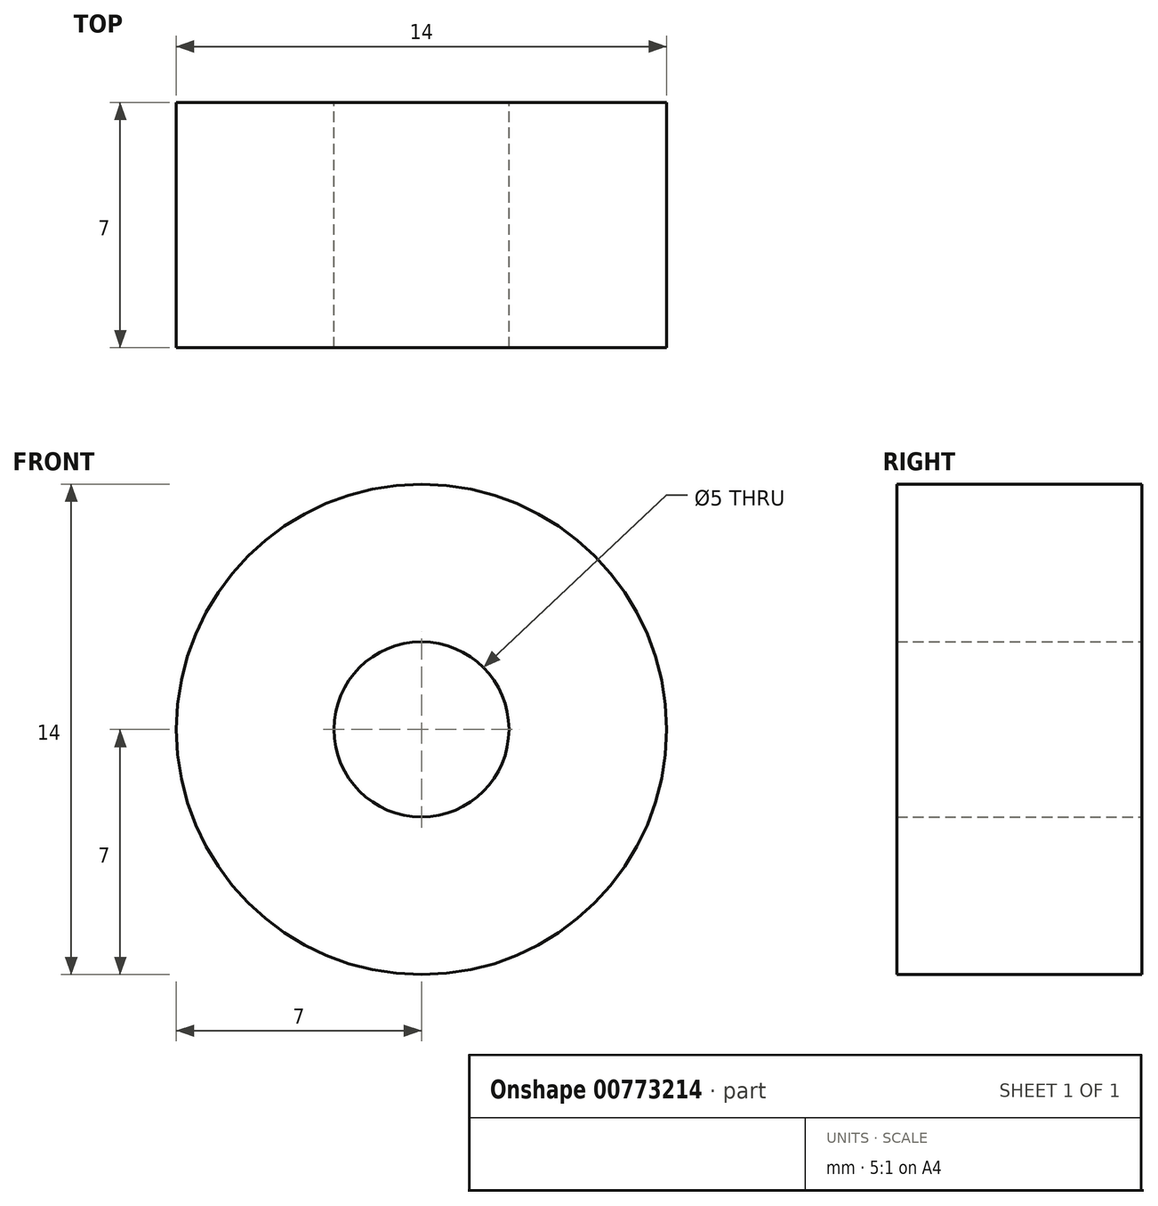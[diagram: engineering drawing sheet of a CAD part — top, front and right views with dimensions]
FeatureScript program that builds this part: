
annotation { "Feature Type Name" : "Feature", "Feature Type Description" : "" }
export const myFeature = defineFeature(function(context is Context, id is Id, definition is map)
    precondition{}
    {
        {
            var Q0;
            Q0=qCreatedBy(makeId("Front.planeOp"),FACE);
            var sketch = newSketch(context, id + "F0", { "sketchPlane" : qUnion([Q0])});
            skCircle(sketch, "E0", {"center": v(0, 0) * mm, "radius": 7 * mm});
            skSolve(sketch);
        }
        {
            var Q0;
            Q0 = qSketchRegion(id + "F0", true);
            extrude(context, id + "F1", {"entities" : qUnion([Q0]), "depth" : 7 * mm, "offsetDistance" : 25 * mm});
        }
        {
            var Q0;
            Q0=qCreatedBy(makeId("Front.planeOp"),FACE);
            var sketch = newSketch(context, id + "F2", { "sketchPlane" : qUnion([Q0])});
            skPoint(sketch, "E1", {"position": v(0, 0) * mm});
            skSolve(sketch);
        }
        {
            var Q0;
            Q0=sQuery(id+"F2.wireOp",VERTEX,"E1");
            var Q1;
            Q1=makeQuery(id+"F1.opExtrude","SWEPT_BODY",BODY,{"disambiguationData":[OSD([sQuery(id+"F0.wireOp",EDGE,"E0")])]});
            hole(context, id + "F3", {"style" : HoleStyle.SIMPLE, "endStyle" : HoleEndStyle.THROUGH, "oppositeDirection" : true, "holeDiameter" : 5 * mm, "majorDiameter" : 5 * mm, "isTappedThrough" : true, "tappedDepth" : 12 * mm, "tapClearance" : 3, "locations" : qUnion([Q0]), "scope" : qUnion([Q1])});
        }
    });
